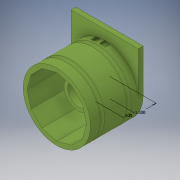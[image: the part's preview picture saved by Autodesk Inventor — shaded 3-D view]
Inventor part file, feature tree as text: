
AUTODESK INVENTOR PART (.ipt)
format: ipt  version: 2018 (Build 220112000, 112)  size: 378,880 bytes
history: native  units: in
note: dims shown in document units (in); Inventor stores cm internally (conversion verified against a paired STEP export)
features: sketch x14, extrude x12, projected_geometry x4, mirror x2, revolve x1
ambient origin geometry x8: Origin, YZ Plane, XZ Plane, XY Plane, X Axis, Y Axis, Z Axis, Center Point
bodies: Solid1 (feature_tree)
feature tree (33):
  extrude  "Extrusion1"  Depth=3.5in
  extrude  "Extrusion2"  Depth=1.75in
  extrude  "Extrusion3"  Depth=0.25in TaperAngle=0.0deg
  extrude  "Extrusion4"  Depth=2.5in TaperAngle=0.0deg
  extrude  "Extrusion6"  Depth=1.5in TaperAngle=0.0deg
  extrude  "Extrusion7"  Depth=1.375in TaperAngle=0.0deg
  revolve  "Revolution1"  [1 undecoded]
  extrude  "Extrusion8"  Depth=3.0in
  extrude  "Extrusion9"  Depth=0.1275in
  sketch  "Sketch11"  dims[d31=0.75in d32=0.625in]
  extrude  "Extrusion10"  Depth=0.75in
  extrude  "Extrusion11"  Depth=0.38in
  extrude  "Extrusion12"  Depth=1.25in
  extrude  "Extrusion13"  Depth=0.75in
  mirror  "Mirror1"
  mirror  "Mirror2"
  sketch  "Sketch1"  dims[d0=3.5in d1=3.5in]
  sketch  "Sketch2"  dims[d2=3.5in d3=1.75in]
  sketch  "Sketch3"  dims[d4=1.75in d5=0.25in d6=0.0in]
  sketch  "Sketch4"  dims[d8=0.0625in d9=2.5in d10=0.0in]
  sketch  "Sketch6"  dims[d11=1.125in d12=1.5in d13=0.0in]
  sketch  "Sketch7"  dims[d14=1.5in d15=1.375in d16=0.0in]
  projected_geometry  "Projected Loop1"
  sketch  "Sketch8"  dims[d21=0.5in d22=1.25in]
  sketch  "Sketch9"  dims[d23=1.0in d24=0.0in d25=3.0in]
  projected_geometry  "Projected Loop2"
  sketch  "Sketch10"  dims[d26=1.0in d27=0.0in d28=0.1275in]
  projected_geometry  "Projected Loop3"
  sketch  "Sketch12"  dims[d33=90.0deg d35=0.38in]
  projected_geometry  "Projected Loop4"
  sketch  "Sketch13"  dims[d36=1.25in d37=1.25in]
  sketch  "Sketch14"  dims[d38=1.0in d39=0.0in d40=0.75in]
  sketch  "Sketch15"  dims[d41=0.125in d42=0.0in d43=1.0in d44=0.5in d45=0.0675in d46=3.5in d47=0.5in d48=0.0in d53=0.2953in d54=0.1181in d55=0.1181in d56=0.2953in d57=14.1732in d59=360.0deg d61=15.0deg d62=0.5256in d63=0.0in d64=0.2135in d69=1.0in d70=0.0in d71=1.25in d72=1.25in d73=1.25in d74=1.25in d75=2.0in d76=1.0in d77=0.3051in d78=0.6102in d79=0.0791in d80=1.0in d81=0.0in]
note: 1 required parameter value undecoded (feature->parameter linkage not recoverable at this tier; creation-order binding heuristic only, values carry confidence <= 0.55)
